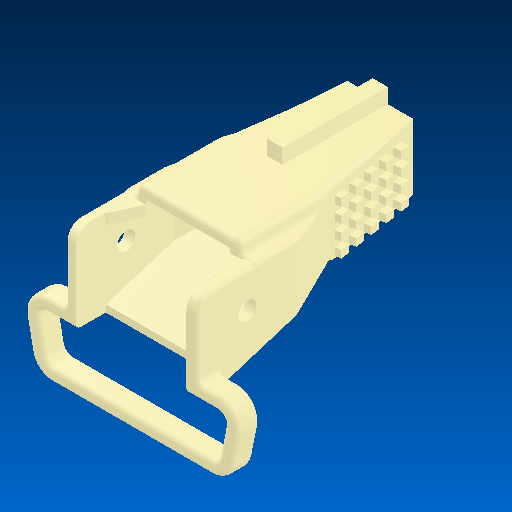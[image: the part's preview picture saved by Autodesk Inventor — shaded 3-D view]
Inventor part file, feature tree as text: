
AUTODESK INVENTOR PART (.ipt)
format: ipt  version: 2025 (Build 290162000, 162)  size: 1,685,504 bytes
history: native  units: mm
features: plane x8, sketch x4, projected_geometry x3, loft x2, extrude x2, mirror x2, split x2, other x2, fillet x1, pattern_linear x1
ambient origin geometry x8: Origin, YZ Plane, XZ Plane, XY Plane, X Axis, Y Axis, Z Axis, Center Point
bodies: Solid1 (feature_tree), Solid2 (feature_tree)
feature tree (27):
  plane  "Work Plane6"
  loft  "Loft3"
  loft  "Loft4"
  fillet  "Fillet6"  Radius=0.25mm
  extrude  "Extrusion35"  Depth=0.5mm TaperAngle=0.0deg
  plane  "Work Plane27"
  extrude  "Extrusion36"  Depth=0.5mm
  pattern_linear  "Rectangular Pattern1"  Spacing1=0.5mm  [1 undecoded]
  plane  "Work Plane29"
  mirror  "Mirror4"
  plane  "Work Plane30"
  mirror  "Mirror5"
  plane  "Work Plane31"
  split  "Split1"
  plane  "Work Plane32"
  split  "Split2"
  plane  "Work Plane4"
  plane  "Work Plane5"
  sketch  "Sketch5"  dims[d23=4.4mm d24=0.0mm d25=90.0deg]
  other  "Edges3"
  sketch  "Sketch7"  dims[d26=0.0mm d27=90.0deg d30=0.0mm d31=90.0deg d447=0.25mm]
  projected_geometry  "Projected Loop54"
  sketch  "Sketch51"  dims[d451=0.5mm d452=1.0mm d453=0.0mm]
  sketch  "Sketch53"  dims[d464=0.6mm d465=0.5mm d466=0.5mm d467=0.0mm d468=100.0mm d470=1.2mm d471=40.0mm d473=1.0mm d474=0.0mm d475=0.0mm d476=90.0deg d39=0.5mm d40=0.872665mm d41=0.5mm d42=0.872665mm d193=0.5mm d194=0.872665mm d195=0.5mm d196=0.872665mm d449=0.5mm d450=0.872665mm]
  projected_geometry  "Projected Loop57"
  projected_geometry  "Projected Loop58"
  other  "Edges4"
note: 1 required parameter value undecoded (feature->parameter linkage not recoverable at this tier; creation-order binding heuristic only, values carry confidence <= 0.55)
